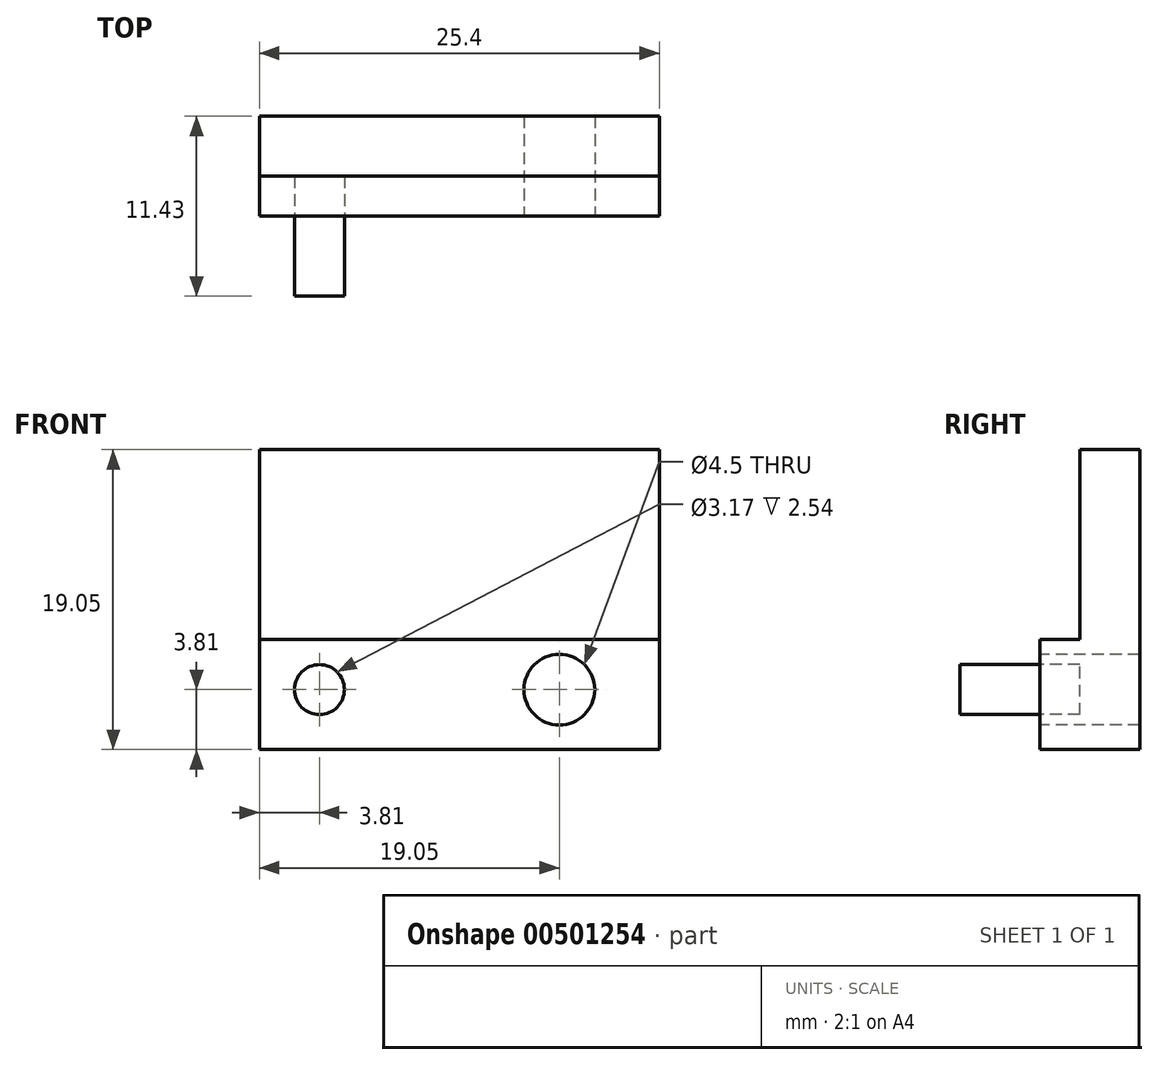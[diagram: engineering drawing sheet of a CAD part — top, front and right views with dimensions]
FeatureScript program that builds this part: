
annotation { "Feature Type Name" : "Feature", "Feature Type Description" : "" }
export const myFeature = defineFeature(function(context is Context, id is Id, definition is map)
    precondition{}
    {
        {
            var Q0;
            Q0=qCreatedBy(makeId("Front.planeOp"),FACE);
            var sketch = newSketch(context, id + "F0", { "sketchPlane" : qUnion([Q0])});
            skLineSegment(sketch, "E0.bottom", {"start": v(0, 0) * mm, "end": v(25.4, 0) * mm});
            skLineSegment(sketch, "E0.top", {"start": v(0, 19.05) * mm, "end": v(25.4, 19.05) * mm});
            skLineSegment(sketch, "E0.left", {"start": v(0, 0) * mm, "end": v(0, 19.05) * mm});
            skLineSegment(sketch, "E0.right", {"start": v(25.4, 0) * mm, "end": v(25.4, 19.05) * mm});
            skSolve(sketch);
        }
        {
            var Q0;
            Q0=makeQuery(id+"F0.imprint","IMPRINT",FACE,{"disambiguationData":[TD([[makeQuery(id+"F0.imprint","IMPRINT",EDGE,{"derivedFrom":sQuery(id+"F0.wireOp",EDGE,"E0.bottom")}),1.0]])]});
            extrude(context, id + "F1", {"entities" : qUnion([Q0]), "depth" : 6.35 * mm});
        }
        {
            var Q0;
            Q0=makeQuery(id+"F1.opExtrude","CAP_FACE",FACE,{"disambiguationData":[OSD([sQuery(id+"F0.wireOp",EDGE,"E0.bottom"),sQuery(id+"F0.wireOp",EDGE,"E0.top"),sQuery(id+"F0.wireOp",EDGE,"E0.left"),sQuery(id+"F0.wireOp",EDGE,"E0.right")])],"isStart":false});
            var sketch = newSketch(context, id + "F2", { "sketchPlane" : qUnion([Q0])});
            skLineSegment(sketch, "E1", {"start": v(0, 0) * mm, "end": v(0, 3.81) * mm});
            skLineSegment(sketch, "E2", {"start": v(0, 3.81) * mm, "end": v(3.81, 3.81) * mm});
            skCircle(sketch, "E3", {"center": v(3.81, 3.81) * mm, "radius": 1.59 * mm});
            skLineSegment(sketch, "E4", {"start": v(25.4, 0) * mm, "end": v(25.4, 3.8) * mm});
            skLineSegment(sketch, "E5", {"start": v(25.4, 3.81) * mm, "end": v(19.05, 3.81) * mm});
            skSolve(sketch);
        }
        {
            var Q0;
            Q0=sQuery(id+"F2.wireOp",VERTEX,"E5.end");
            var Q1;
            Q1=makeQuery(id+"F1.opExtrude","SWEPT_BODY",BODY,{"disambiguationData":[OSD([sQuery(id+"F0.wireOp",EDGE,"E0.bottom"),sQuery(id+"F0.wireOp",EDGE,"E0.top"),sQuery(id+"F0.wireOp",EDGE,"E0.left"),sQuery(id+"F0.wireOp",EDGE,"E0.right")])]});
            hole(context, id + "F3", {"style" : HoleStyle.SIMPLE, "endStyle" : HoleEndStyle.THROUGH, "standardTappedOrClearance" : lookupTablePath({ "standard" : "ANSI", "fit" : "Normal (ASME)", "size" : "#8", "type" : "Clearance" }), "standardBlindInLast" : lookupTablePath({ "fit" : "Free", "standard" : "ANSI", "size" : "#8", "type" : "Clearance" }), "holeDiameter" : 4.5 * mm, "isTappedThrough" : true, "tappedDepth" : 12.7 * mm, "tapClearance" : 3, "locations" : qUnion([Q0]), "scope" : qUnion([Q1])});
        }
        {
            var Q0;
            Q0=makeQuery(id+"F2.imprint","IMPRINT",FACE,{"disambiguationData":[TD([[makeQuery(id+"F2.imprint","IMPRINT",EDGE,{"derivedFrom":sQuery(id+"F2.wireOp",EDGE,"E3")}),1.0]])]});
            extrude(context, id + "F4", {"entities" : qUnion([Q0]), "operationType" : NewBodyOperationType.ADD, "depth" : 5.08 * mm});
        }
        {
            var Q0;
            {var subQ1=sQuery(id+"F2.wireOp",EDGE,"E1");Q0=makeQuery(id+"F2.imprint","IMPRINT",FACE,{"disambiguationData":[TD([[makeQuery(id+"F2.imprint","IMPRINT",EDGE,{"derivedFrom":subQ1}),-1.0]])]});}
            var sketch = newSketch(context, id + "F5", { "sketchPlane" : qUnion([Q0])});
            skLineSegment(sketch, "E6.0", {"start": v(0, 0) * mm, "end": v(0, 3.81) * mm});
            skLineSegment(sketch, "E6.1", {"start": v(0, 3.81) * mm, "end": v(3.81, 3.81) * mm});
            skCircle(sketch, "E6.2", {"center": v(3.81, 3.81) * mm, "radius": 1.59 * mm});
            skLineSegment(sketch, "E6.3", {"start": v(25.4, 0) * mm, "end": v(25.4, 3.8) * mm});
            skLineSegment(sketch, "E6.4", {"start": v(25.4, 3.81) * mm, "end": v(19.05, 3.81) * mm});
            skCircle(sketch, "E6.5", {"center": v(19.05, 3.81) * mm, "radius": 2.25 * mm});
            skLineSegment(sketch, "E7", {"start": v(19.05, 3.81) * mm, "end": v(19.05, 6.99) * mm});
            skLineSegment(sketch, "E8", {"start": v(19.05, 6.99) * mm, "end": v(38.13, 6.99) * mm});
            skLineSegment(sketch, "E9.0", {"start": v(0, 19.05) * mm, "end": v(25.4, 19.05) * mm});
            skLineSegment(sketch, "E10.0", {"start": v(0, 0) * mm, "end": v(0, 19.05) * mm});
            skLineSegment(sketch, "E11", {"start": v(38.13, 6.99) * mm, "end": v(25.4, 19.05) * mm});
            skLineSegment(sketch, "E12", {"start": v(0, 19.05) * mm, "end": v(0, 6.99) * mm});
            skLineSegment(sketch, "E13", {"start": v(0, 6.99) * mm, "end": v(19.05, 6.99) * mm});
            skSolve(sketch);
        }
        {
            var Q0;
            Q0 = qSketchRegion(id + "F5", true);
            extrude(context, id + "F6", {"entities" : qUnion([Q0]), "operationType" : NewBodyOperationType.REMOVE, "oppositeDirection" : true, "depth" : 2.54 * mm});
        }
    });
